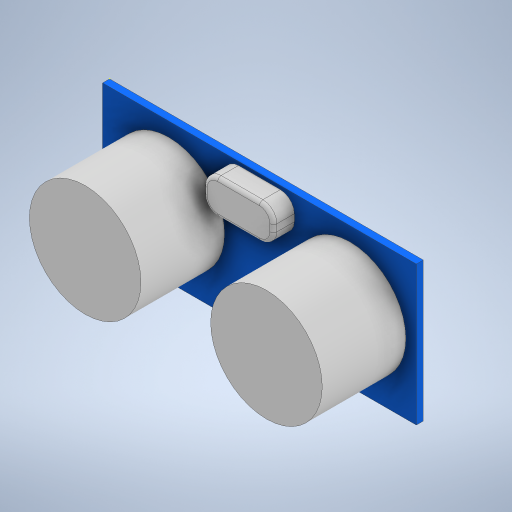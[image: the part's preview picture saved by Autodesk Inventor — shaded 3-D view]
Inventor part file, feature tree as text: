
AUTODESK INVENTOR PART (.ipt)
format: ipt  version: 2024.2 (Build 282272000, 272)  size: 324,096 bytes
history: native  units: mm
features: sketch x5, extrude x4, fillet x2
ambient origin geometry x8: Origin, YZ Plane, XZ Plane, XY Plane, X Axis, Y Axis, Z Axis, Center Point
bodies: Solid1 (feature_tree)
feature tree (11):
  extrude  "Extrusion1"  Depth=20.0mm
  extrude  "Extrusion2"  Depth=1.0mm
  extrude  "Extrusion3"  Depth=10.0mm
  fillet  "Fillet1"  Radius=10.0mm
  fillet  "Fillet2"  Radius=9.5mm
  sketch  "Sketch4"  dims[d9=12.0mm d10=0.0mm d11=10.0mm]
  extrude  "Extrusion4"  Depth=10.0mm
  sketch  "Sketch1"  dims[d0=45.0mm d1=20.0mm]
  sketch  "Sketch2"  dims[d2=1.0mm d3=0.0mm d4=16.0mm]
  sketch  "Sketch3"  dims[d5=16.0mm d6=26.0mm d7=10.0mm d8=9.5mm]
  sketch  "Sketch5"  dims[d12=5.0mm d13=17.5mm d14=0.5mm d15=3.0mm d16=0.0mm d17=2.0mm d18=0.5mm d19=2.5mm d20=10.0mm d21=17.5mm d22=10.0mm d23=0.0mm]
